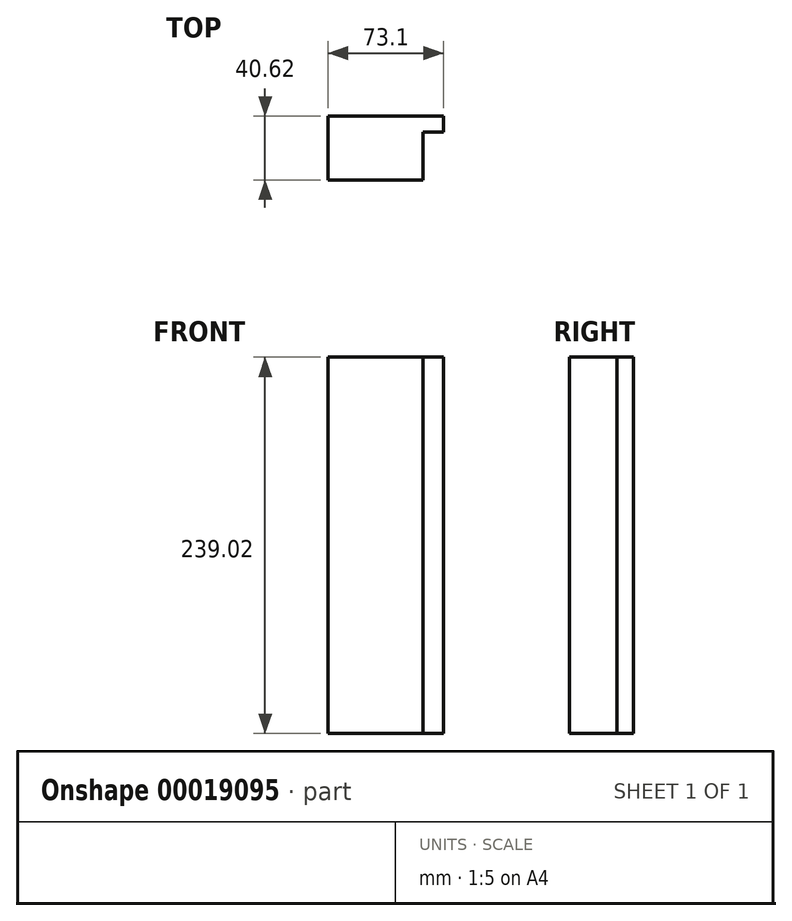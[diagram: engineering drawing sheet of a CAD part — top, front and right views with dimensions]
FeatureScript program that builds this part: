
annotation { "Feature Type Name" : "Feature", "Feature Type Description" : "" }
export const myFeature = defineFeature(function(context is Context, id is Id, definition is map)
    precondition{}
    {
        {
            var Q0;
            Q0=qCreatedBy(makeId("Top.planeOp"),FACE);
            var sketch = newSketch(context, id + "F0", { "sketchPlane" : qUnion([Q0])});
            skLineSegment(sketch, "E0.bottom", {"start": v(-41.3, 19.36) * mm, "end": v(31.8, 19.36) * mm});
            skLineSegment(sketch, "E0.top", {"start": v(-41.3, -21.26) * mm, "end": v(31.8, -21.26) * mm});
            skLineSegment(sketch, "E0.left", {"start": v(-41.3, 19.36) * mm, "end": v(-41.3, -21.26) * mm});
            skLineSegment(sketch, "E0.right", {"start": v(31.8, 19.36) * mm, "end": v(31.8, -21.26) * mm});
            skLineSegment(sketch, "E1.bottom", {"start": v(31.8, -21.26) * mm, "end": v(18.75, -21.26) * mm});
            skLineSegment(sketch, "E1.top", {"start": v(31.8, 9.16) * mm, "end": v(18.75, 9.16) * mm});
            skLineSegment(sketch, "E1.left", {"start": v(31.8, -21.26) * mm, "end": v(31.8, 9.16) * mm});
            skLineSegment(sketch, "E1.right", {"start": v(18.75, -21.26) * mm, "end": v(18.75, 9.16) * mm});
            skSolve(sketch);
        }
        {
            var Q0;
            Q0=makeQuery(id+"F0.imprint","IMPRINT",FACE,{"disambiguationData":[TD([[makeQuery(id+"F0.imprint","IMPRINT",EDGE,{"derivedFrom":sQuery(id+"F0.wireOp",EDGE,"E0.bottom")}),-1.0]])]});
            extrude(context, id + "F1", {"entities" : qUnion([Q0]), "oppositeDirection" : true, "depth" : 239.02 * mm});
        }
    });
